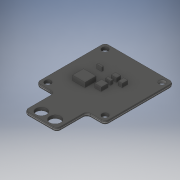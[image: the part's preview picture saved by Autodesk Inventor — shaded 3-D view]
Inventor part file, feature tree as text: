
AUTODESK INVENTOR PART (.ipt)
format: ipt  version: 2019 (Build 230136000, 136)  size: 233,984 bytes
history: mixed  units: mm
features: sketch x2, other x2, extrude x1, projected_geometry x1, imported_body x1
ambient origin geometry x8: Origin, YZ Plane, XZ Plane, XY Plane, X Axis, Y Axis, Z Axis, Center Point
bodies: Body1 (imported_parasolid)
feature tree (7):
  sketch  "Эскиз1"
  extrude  "Выдавливание1"  Depth=14.75mm TaperAngle=0.0deg
  other  "Твердое тело4"
  projected_geometry  "Спроецированная петля1"
  sketch  "Эскиз2"
  other  "Boss.-Extru.3"
  imported_body  NMx_Import_Brep_tag  [imported B-rep: ~86 faces, bbox_mm=[36.2, 4.1, 52.0]]
